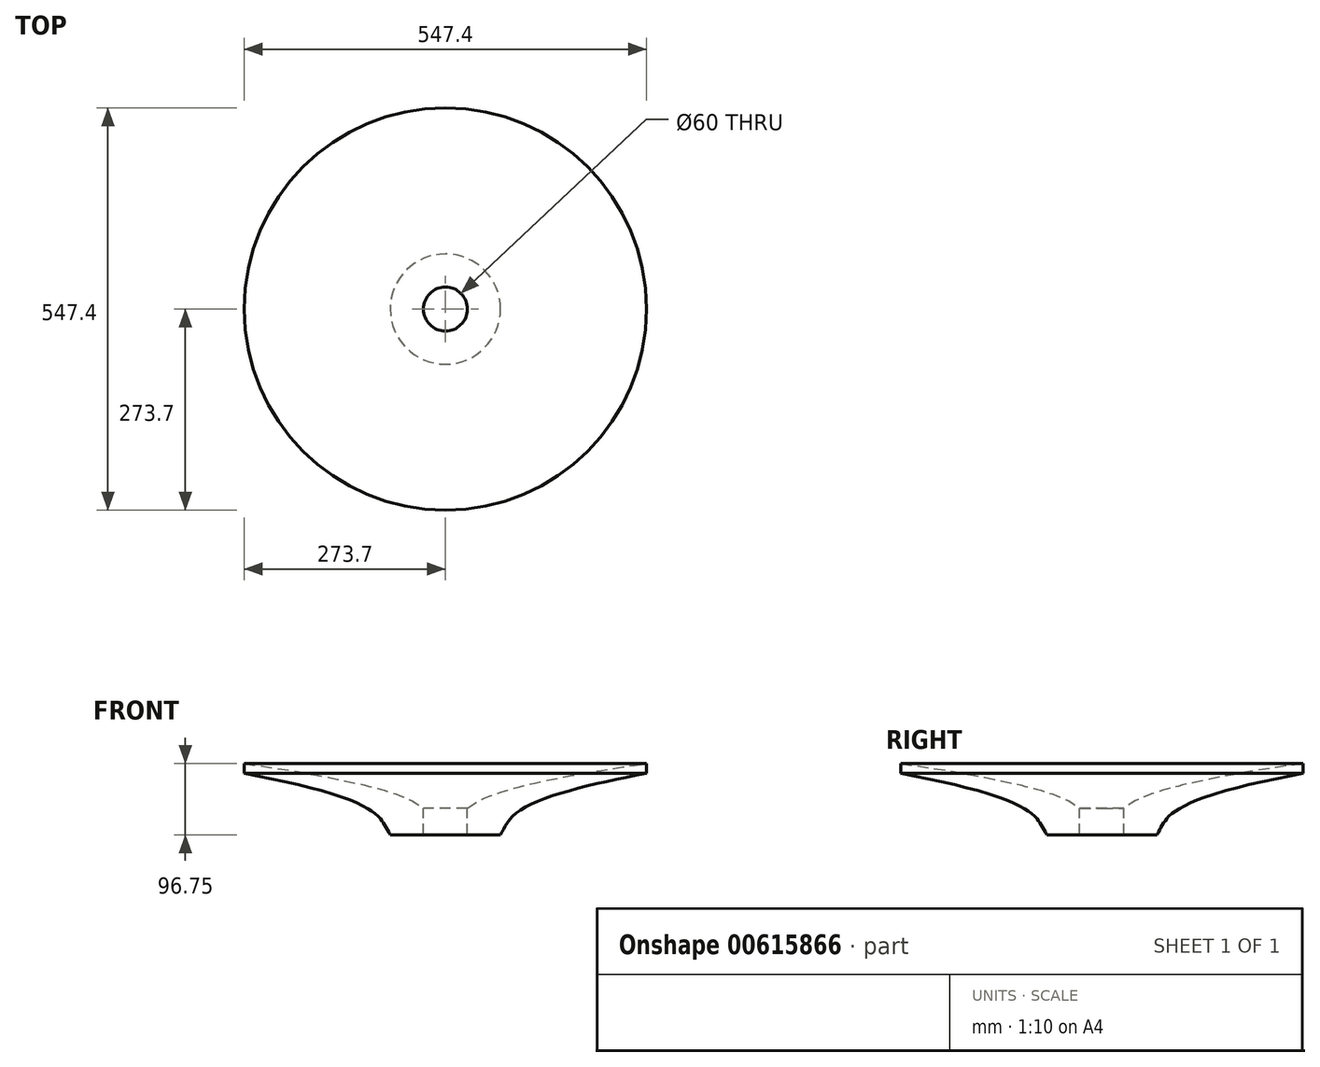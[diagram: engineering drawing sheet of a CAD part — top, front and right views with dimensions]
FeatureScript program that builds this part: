
annotation { "Feature Type Name" : "Feature", "Feature Type Description" : "" }
export const myFeature = defineFeature(function(context is Context, id is Id, definition is map)
    precondition{}
    {
        {
            var Q0;
            Q0=qCreatedBy(makeId("Front.planeOp"),FACE);
            var sketch = newSketch(context, id + "F0", { "sketchPlane" : qUnion([Q0])});
            skPoint(sketch, "E0", {"position": v(-30, -96.75) * mm});
            skPoint(sketch, "E1", {"position": v(-273.7, 0) * mm});
            skLineSegment(sketch, "E2", {"start": v(-30, -96.75) * mm, "end": v(-75, -96.75) * mm});
            skLineSegment(sketch, "E3", {"start": v(-30, -96.75) * mm, "end": v(-30, -60.75) * mm});
            skPoint(sketch, "E4", {"position": v(-97, -66.75) * mm});
            skLineSegment(sketch, "E5", {"start": v(-273.7, 0) * mm, "end": v(-273.7, -13) * mm});
            skFitSpline(sketch, "E6", {"points": [v(-75, -96.75) * mm, v(-97, -66.75) * mm, v(-273.7, -13) * mm], "startDerivative": vector(-48.42, 82.32) * mm, "endDerivative": vector(-319.46, 61.94) * mm});
            skPoint(sketch, "E7", {"position": v(-85, -35.75) * mm});
            skFitSpline(sketch, "E8", {"points": [v(-30, -60.75) * mm, v(-85, -35.75) * mm, v(-273.7, 0) * mm], "startDerivative": vector(-121.06, 96.01) * mm, "endDerivative": vector(-374.6, 50.34) * mm});
            skLineSegment(sketch, "E9", {"start": v(0, 0) * mm, "end": v(0, -171.2) * mm});
            skSolve(sketch);
        }
        {
            var Q0;
            Q0=makeQuery(id+"F0.imprint","IMPRINT",FACE,{"disambiguationData":[TD([[makeQuery(id+"F0.imprint","IMPRINT",EDGE,{"derivedFrom":sQuery(id+"F0.wireOp",EDGE,"E2")}),-1.0]])]});
            var Q1;
            Q1=sQuery(id+"F0.wireOp",EDGE,"E9");
            revolve(context, id + "F1", {"entities" : qUnion([Q0]), "axis" : qUnion([Q1]), "revolveType" : RevolveType.FULL});
        }
    });
